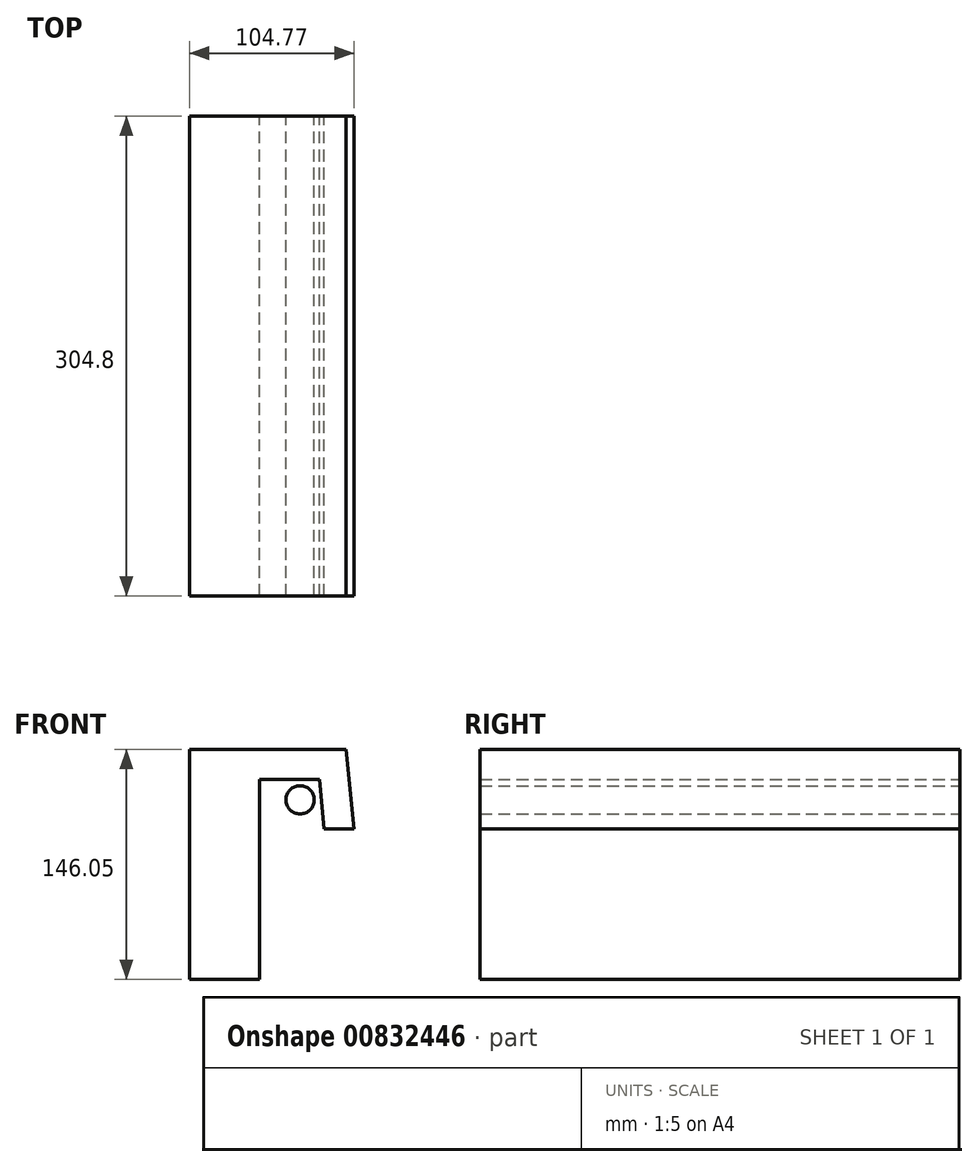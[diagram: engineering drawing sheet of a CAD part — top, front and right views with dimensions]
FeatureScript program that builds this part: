
annotation { "Feature Type Name" : "Feature", "Feature Type Description" : "" }
export const myFeature = defineFeature(function(context is Context, id is Id, definition is map)
    precondition{}
    {
        {
            var Q0;
            Q0=qCreatedBy(makeId("Front.planeOp"),FACE);
            var sketch = newSketch(context, id + "F0", { "sketchPlane" : qUnion([Q0])});
            skLineSegment(sketch, "E0.bottom", {"start": v(0, 0) * mm, "end": v(-44.45, 0) * mm});
            skLineSegment(sketch, "E0.top", {"start": v(0, -127) * mm, "end": v(-44.45, -127) * mm});
            skLineSegment(sketch, "E0.left", {"start": v(0, 0) * mm, "end": v(0, -127) * mm});
            skLineSegment(sketch, "E0.right", {"start": v(-44.45, 0) * mm, "end": v(-44.45, -127) * mm});
            skLineSegment(sketch, "E1.bottom", {"start": v(-44.45, 0) * mm, "end": v(38.1, 0) * mm});
            skLineSegment(sketch, "E1.top", {"start": v(-44.45, 19.05) * mm, "end": v(36.18, 19.05) * mm});
            skLineSegment(sketch, "E1.left", {"start": v(-44.45, 0) * mm, "end": v(-44.45, 19.05) * mm});
            skLineSegment(sketch, "E1.right", {"start": v(38.1, 0) * mm, "end": v(36.18, 19.05) * mm});
            skLineSegment(sketch, "E2.bottom", {"start": v(0, 0) * mm, "end": v(12.7, 0) * mm});
            skLineSegment(sketch, "E2.top", {"start": v(0, -127) * mm, "end": v(12.7, -127) * mm});
            skLineSegment(sketch, "E2.right", {"start": v(12.7, 0) * mm, "end": v(12.7, -127) * mm});
            skLineSegment(sketch, "E3", {"start": v(36.18, 19.05) * mm, "end": v(41.27, -31.5) * mm});
            skLineSegment(sketch, "E4", {"start": v(41.27, -31.5) * mm, "end": v(60.32, -31.5) * mm});
            skLineSegment(sketch, "E5", {"start": v(60.32, -31.5) * mm, "end": v(55.23, 19.05) * mm});
            skLineSegment(sketch, "E6", {"start": v(55.23, 19.05) * mm, "end": v(36.18, 19.05) * mm});
            skCircle(sketch, "E7", {"center": v(25.9, -12.94) * mm, "radius": 8.97 * mm});
            skSolve(sketch);
        }
        {
            var Q0;
            Q0=makeQuery(id+"F0.imprint","IMPRINT",FACE,{"disambiguationData":[TD([[makeQuery(id+"F0.imprint","IMPRINT",EDGE,{"derivedFrom":sQuery(id+"F0.wireOp",EDGE,"E0.top")}),-1.0]])]});
            var Q1;
            {var subQ0=sQuery(id+"F0.wireOp",EDGE,"E4");Q1=makeQuery(id+"F0.imprint","IMPRINT",FACE,{"disambiguationData":[TD([[makeQuery(id+"F0.imprint","IMPRINT",EDGE,{"derivedFrom":subQ0}),1.0]])]});}
            var Q2;
            {var subQ1=sQuery(id+"F0.wireOp",EDGE,"E1.top");Q2=makeQuery(id+"F0.imprint","IMPRINT",FACE,{"disambiguationData":[TD([[makeQuery(id+"F0.imprint","IMPRINT",EDGE,{"derivedFrom":subQ1}),-1.0]])]});}
            var Q3;
            Q3=makeQuery(id+"F0.imprint","IMPRINT",FACE,{"disambiguationData":[TD([[makeQuery(id+"F0.imprint","IMPRINT",EDGE,{"derivedFrom":sQuery(id+"F0.wireOp",EDGE,"E2.bottom")}),-1.0]])]});
            var Q4;
            Q4=makeQuery(id+"F0.imprint","IMPRINT",FACE,{"disambiguationData":[TD([[makeQuery(id+"F0.imprint","IMPRINT",EDGE,{"derivedFrom":sQuery(id+"F0.wireOp",EDGE,"E7")}),1.0]])]});
            extrude(context, id + "F1", {"entities" : qUnion([Q0, Q1, Q2, Q3, Q4]), "depth" : 304.8 * mm, "offsetDistance" : 25.4 * mm});
        }
    });
